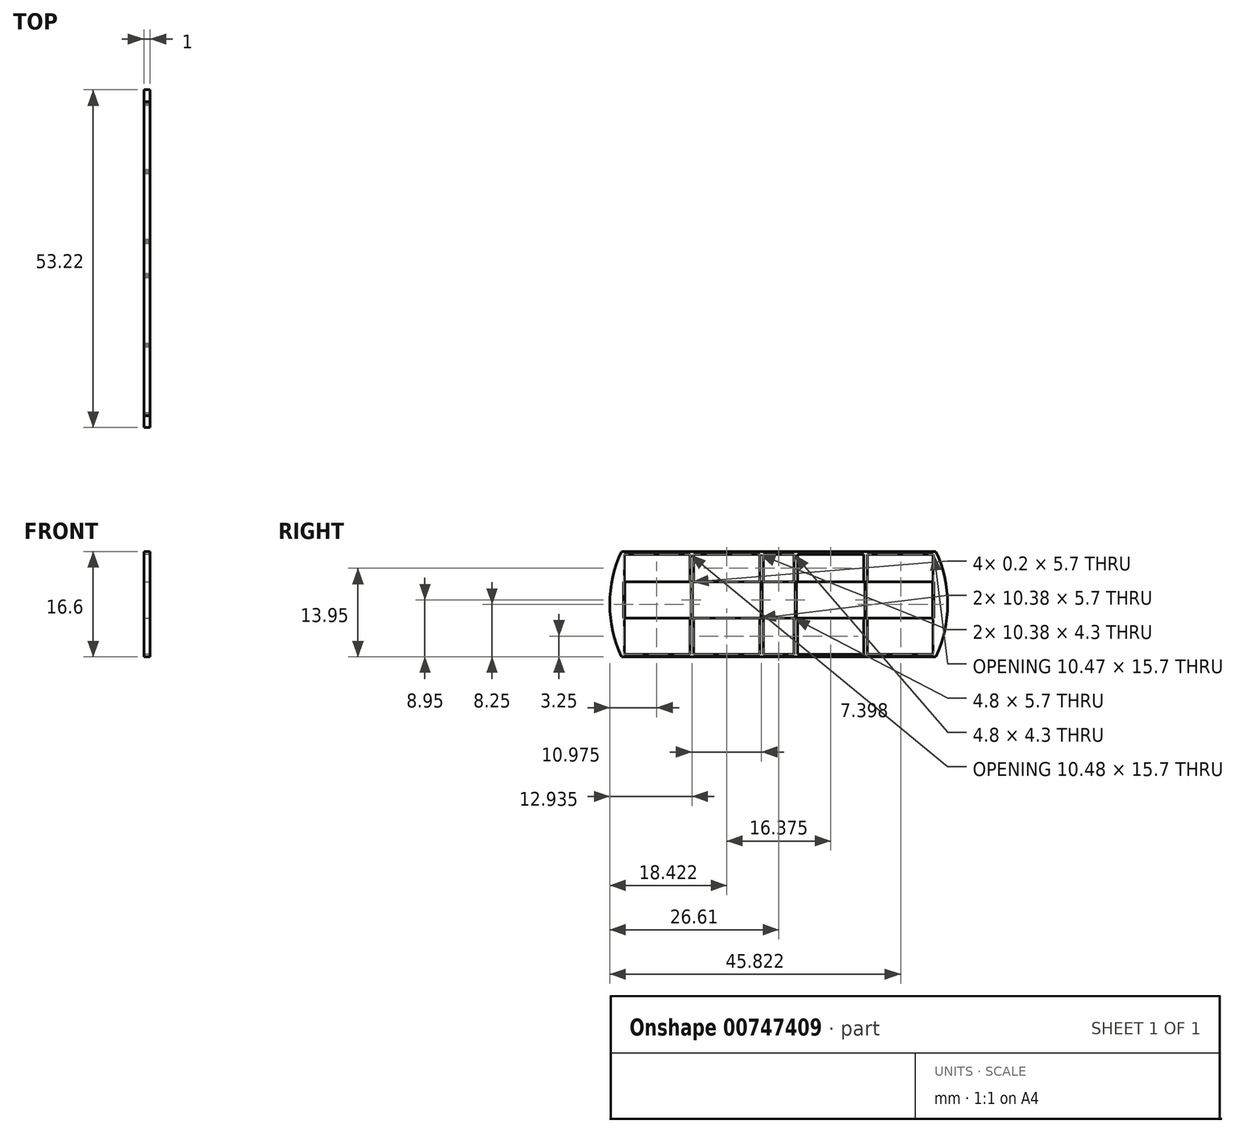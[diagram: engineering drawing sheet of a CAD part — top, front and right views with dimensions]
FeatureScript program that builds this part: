
annotation { "Feature Type Name" : "Feature", "Feature Type Description" : "" }
export const myFeature = defineFeature(function(context is Context, id is Id, definition is map)
    precondition{}
    {
        {
            var Q0;
            Q0=qCreatedBy(makeId("Right.planeOp"),FACE);
            var sketch = newSketch(context, id + "F0", { "sketchPlane" : qUnion([Q0])});
            skLineSegment(sketch, "E0.bottom", {"start": v(0, 0) * mm, "end": v(-49.5, 0) * mm});
            skLineSegment(sketch, "E0.top", {"start": v(0, 16.6) * mm, "end": v(-49.5, 16.6) * mm});
            skLineSegment(sketch, "E0.left", {"start": v(0, 0) * mm, "end": v(0, 16.6) * mm, "construction": true});
            skLineSegment(sketch, "E0.right", {"start": v(-49.5, 0) * mm, "end": v(-49.5, 16.6) * mm, "construction": true});
            skArc(sketch, "E1", {"start": v(-49.5, 0) * mm, "mid": v(-51.36, 8.3) * mm, "end": v(-49.5, 16.6) * mm});
            skPoint(sketch, "E1.centerSnap0", {"position": v(-49.5, 8.3) * mm});
            skArc(sketch, "E2", {"start": v(0, 0) * mm, "mid": v(1.86, 8.3) * mm, "end": v(0, 16.6) * mm});
            skPoint(sketch, "E2.centerSnap0", {"position": v(0, 8.3) * mm});
            skLineSegment(sketch, "E3", {"start": v(-49.5, 8.3) * mm, "end": v(-51.36, 8.3) * mm, "construction": true});
            skLineSegment(sketch, "E4", {"start": v(0, 8.3) * mm, "end": v(1.86, 8.3) * mm, "construction": true});
            skLineSegment(sketch, "E5.bottom", {"start": v(-49.1, 16.1) * mm, "end": v(-38.73, 16.1) * mm});
            skLineSegment(sketch, "E5.top", {"start": v(-49.1, 11.8) * mm, "end": v(-38.73, 11.8) * mm});
            skLineSegment(sketch, "E5.left", {"start": v(-49.1, 16.1) * mm, "end": v(-49.1, 11.8) * mm});
            skLineSegment(sketch, "E5.right", {"start": v(-38.73, 16.1) * mm, "end": v(-38.73, 11.8) * mm});
            skLineSegment(sketch, "E6.bottom", {"start": v(-38.12, 16.1) * mm, "end": v(-27.75, 16.1) * mm});
            skLineSegment(sketch, "E6.top", {"start": v(-38.12, 11.8) * mm, "end": v(-27.75, 11.8) * mm});
            skLineSegment(sketch, "E6.left", {"start": v(-38.12, 16.1) * mm, "end": v(-38.12, 11.8) * mm});
            skLineSegment(sketch, "E6.right", {"start": v(-27.75, 16.1) * mm, "end": v(-27.75, 11.8) * mm});
            skLineSegment(sketch, "E7.bottom", {"start": v(-27.15, 16.1) * mm, "end": v(-22.35, 16.1) * mm});
            skLineSegment(sketch, "E7.top", {"start": v(-27.15, 11.8) * mm, "end": v(-22.35, 11.8) * mm});
            skLineSegment(sketch, "E7.left", {"start": v(-27.15, 16.1) * mm, "end": v(-27.15, 11.8) * mm});
            skLineSegment(sketch, "E7.right", {"start": v(-22.35, 16.1) * mm, "end": v(-22.35, 11.8) * mm});
            skLineSegment(sketch, "E8.bottom", {"start": v(-21.75, 16.1) * mm, "end": v(-11.38, 16.1) * mm});
            skLineSegment(sketch, "E8.top", {"start": v(-21.75, 11.8) * mm, "end": v(-11.38, 11.8) * mm});
            skLineSegment(sketch, "E8.left", {"start": v(-21.75, 16.1) * mm, "end": v(-21.75, 11.8) * mm});
            skLineSegment(sketch, "E8.right", {"start": v(-11.38, 16.1) * mm, "end": v(-11.38, 11.8) * mm});
            skLineSegment(sketch, "E9.bottom", {"start": v(-10.78, 16.1) * mm, "end": v(-0.4, 16.1) * mm});
            skLineSegment(sketch, "E9.top", {"start": v(-10.78, 11.8) * mm, "end": v(-0.4, 11.8) * mm});
            skLineSegment(sketch, "E9.left", {"start": v(-10.78, 16.1) * mm, "end": v(-10.78, 11.8) * mm});
            skLineSegment(sketch, "E9.right", {"start": v(-0.4, 16.1) * mm, "end": v(-0.4, 11.8) * mm});
            skLineSegment(sketch, "E10.bottom", {"start": v(-49.1, 6.1) * mm, "end": v(-38.73, 6.1) * mm});
            skLineSegment(sketch, "E10.top", {"start": v(-49.1, 0.4) * mm, "end": v(-38.73, 0.4) * mm});
            skLineSegment(sketch, "E10.left", {"start": v(-49.1, 6.1) * mm, "end": v(-49.1, 0.4) * mm});
            skLineSegment(sketch, "E10.right", {"start": v(-38.73, 6.1) * mm, "end": v(-38.73, 0.4) * mm});
            skLineSegment(sketch, "E11.bottom", {"start": v(-38.12, 6.1) * mm, "end": v(-27.75, 6.1) * mm});
            skLineSegment(sketch, "E11.top", {"start": v(-38.12, 0.4) * mm, "end": v(-27.75, 0.4) * mm});
            skLineSegment(sketch, "E11.left", {"start": v(-38.12, 6.1) * mm, "end": v(-38.12, 0.4) * mm});
            skLineSegment(sketch, "E11.right", {"start": v(-27.75, 6.1) * mm, "end": v(-27.75, 0.4) * mm});
            skLineSegment(sketch, "E12.bottom", {"start": v(-27.15, 6.1) * mm, "end": v(-22.35, 6.1) * mm});
            skLineSegment(sketch, "E12.top", {"start": v(-27.15, 0.4) * mm, "end": v(-22.35, 0.4) * mm});
            skLineSegment(sketch, "E12.left", {"start": v(-27.15, 6.1) * mm, "end": v(-27.15, 0.4) * mm});
            skLineSegment(sketch, "E12.right", {"start": v(-22.35, 6.1) * mm, "end": v(-22.35, 0.4) * mm});
            skLineSegment(sketch, "E13.bottom", {"start": v(-21.75, 6.1) * mm, "end": v(-11.38, 6.1) * mm});
            skLineSegment(sketch, "E13.top", {"start": v(-21.75, 0.4) * mm, "end": v(-11.38, 0.4) * mm});
            skLineSegment(sketch, "E13.left", {"start": v(-21.75, 6.1) * mm, "end": v(-21.75, 0.4) * mm});
            skLineSegment(sketch, "E13.right", {"start": v(-11.38, 6.1) * mm, "end": v(-11.38, 0.4) * mm});
            skLineSegment(sketch, "E14.bottom", {"start": v(-10.78, 6.1) * mm, "end": v(-0.4, 6.1) * mm});
            skLineSegment(sketch, "E14.top", {"start": v(-10.78, 0.4) * mm, "end": v(-0.4, 0.4) * mm});
            skLineSegment(sketch, "E14.left", {"start": v(-10.78, 6.1) * mm, "end": v(-10.78, 0.4) * mm});
            skLineSegment(sketch, "E14.right", {"start": v(-0.4, 6.1) * mm, "end": v(-0.4, 0.4) * mm});
            skLineSegment(sketch, "E15", {"start": v(-38.73, 13.95) * mm, "end": v(-38.12, 13.95) * mm, "construction": true});
            skLineSegment(sketch, "E16", {"start": v(-27.75, 13.95) * mm, "end": v(-27.15, 13.95) * mm, "construction": true});
            skLineSegment(sketch, "E17", {"start": v(-22.35, 13.95) * mm, "end": v(-21.75, 13.95) * mm, "construction": true});
            skLineSegment(sketch, "E18", {"start": v(-11.38, 13.95) * mm, "end": v(-10.78, 13.95) * mm, "construction": true});
            skSolve(sketch);
        }
        {
            var Q0;
            Q0 = qSketchRegion(id + "F0", true);
            extrude(context, id + "F1", {"entities" : qUnion([Q0]), "depth" : 1 * mm, "offsetDistance" : 25 * mm});
        }
        {
            var Q0;
            Q0=makeQuery(id+"F1.opExtrude","CAP_FACE",FACE,{"disambiguationData":[OSD([sQuery(id+"F0.wireOp",EDGE,"E0.bottom"),sQuery(id+"F0.wireOp",EDGE,"E0.top"),sQuery(id+"F0.wireOp",EDGE,"E1"),sQuery(id+"F0.wireOp",EDGE,"E2"),sQuery(id+"F0.wireOp",EDGE,"E5.bottom"),sQuery(id+"F0.wireOp",EDGE,"E5.top"),sQuery(id+"F0.wireOp",EDGE,"E5.left"),sQuery(id+"F0.wireOp",EDGE,"E5.right"),sQuery(id+"F0.wireOp",EDGE,"E6.bottom"),sQuery(id+"F0.wireOp",EDGE,"E6.top"),sQuery(id+"F0.wireOp",EDGE,"E6.left"),sQuery(id+"F0.wireOp",EDGE,"E6.right"),sQuery(id+"F0.wireOp",EDGE,"E7.bottom"),sQuery(id+"F0.wireOp",EDGE,"E7.top"),sQuery(id+"F0.wireOp",EDGE,"E7.left"),sQuery(id+"F0.wireOp",EDGE,"E7.right"),sQuery(id+"F0.wireOp",EDGE,"E8.bottom"),sQuery(id+"F0.wireOp",EDGE,"E8.top"),sQuery(id+"F0.wireOp",EDGE,"E8.left"),sQuery(id+"F0.wireOp",EDGE,"E8.right"),sQuery(id+"F0.wireOp",EDGE,"E9.bottom"),sQuery(id+"F0.wireOp",EDGE,"E9.top"),sQuery(id+"F0.wireOp",EDGE,"E9.left"),sQuery(id+"F0.wireOp",EDGE,"E9.right"),sQuery(id+"F0.wireOp",EDGE,"E10.bottom"),sQuery(id+"F0.wireOp",EDGE,"E10.top"),sQuery(id+"F0.wireOp",EDGE,"E10.left"),sQuery(id+"F0.wireOp",EDGE,"E10.right"),sQuery(id+"F0.wireOp",EDGE,"E11.bottom"),sQuery(id+"F0.wireOp",EDGE,"E11.top"),sQuery(id+"F0.wireOp",EDGE,"E11.left"),sQuery(id+"F0.wireOp",EDGE,"E11.right"),sQuery(id+"F0.wireOp",EDGE,"E12.bottom"),sQuery(id+"F0.wireOp",EDGE,"E12.top"),sQuery(id+"F0.wireOp",EDGE,"E12.left"),sQuery(id+"F0.wireOp",EDGE,"E12.right"),sQuery(id+"F0.wireOp",EDGE,"E13.bottom"),sQuery(id+"F0.wireOp",EDGE,"E13.top"),sQuery(id+"F0.wireOp",EDGE,"E13.left"),sQuery(id+"F0.wireOp",EDGE,"E13.right"),sQuery(id+"F0.wireOp",EDGE,"E14.bottom"),sQuery(id+"F0.wireOp",EDGE,"E14.top"),sQuery(id+"F0.wireOp",EDGE,"E14.left"),sQuery(id+"F0.wireOp",EDGE,"E14.right")])],"isStart":false});
            var sketch = newSketch(context, id + "F2", { "sketchPlane" : qUnion([Q0])});
            skLineSegment(sketch, "E19.bottom", {"start": v(-49.2, 11.8) * mm, "end": v(-49, 11.8) * mm});
            skLineSegment(sketch, "E19.top", {"start": v(-49.2, 6.1) * mm, "end": v(-49, 6.1) * mm});
            skLineSegment(sketch, "E19.left", {"start": v(-49.2, 11.8) * mm, "end": v(-49.2, 6.1) * mm});
            skLineSegment(sketch, "E19.right", {"start": v(-49, 11.8) * mm, "end": v(-49, 6.1) * mm});
            skLineSegment(sketch, "E20.bottom", {"start": v(-38.32, 11.8) * mm, "end": v(-38.53, 11.8) * mm});
            skLineSegment(sketch, "E20.top", {"start": v(-38.32, 6.1) * mm, "end": v(-38.53, 6.1) * mm});
            skLineSegment(sketch, "E20.left", {"start": v(-38.32, 11.8) * mm, "end": v(-38.32, 6.1) * mm});
            skLineSegment(sketch, "E20.right", {"start": v(-38.53, 11.8) * mm, "end": v(-38.53, 6.1) * mm});
            skLineSegment(sketch, "E21.bottom", {"start": v(-27.35, 11.8) * mm, "end": v(-27.55, 11.8) * mm});
            skLineSegment(sketch, "E21.top", {"start": v(-27.35, 6.1) * mm, "end": v(-27.55, 6.1) * mm});
            skLineSegment(sketch, "E21.left", {"start": v(-27.35, 11.8) * mm, "end": v(-27.35, 6.1) * mm});
            skLineSegment(sketch, "E21.right", {"start": v(-27.55, 11.8) * mm, "end": v(-27.55, 6.1) * mm});
            skLineSegment(sketch, "E22.bottom", {"start": v(-21.95, 11.8) * mm, "end": v(-22.15, 11.8) * mm});
            skLineSegment(sketch, "E22.top", {"start": v(-21.95, 6.1) * mm, "end": v(-22.15, 6.1) * mm});
            skLineSegment(sketch, "E22.left", {"start": v(-22.15, 11.8) * mm, "end": v(-22.15, 6.1) * mm});
            skLineSegment(sketch, "E22.right", {"start": v(-21.95, 11.8) * mm, "end": v(-21.95, 6.1) * mm});
            skLineSegment(sketch, "E23.bottom", {"start": v(-10.98, 11.8) * mm, "end": v(-11.18, 11.8) * mm});
            skLineSegment(sketch, "E23.top", {"start": v(-10.97, 6.1) * mm, "end": v(-11.17, 6.1) * mm});
            skLineSegment(sketch, "E23.left", {"start": v(-10.98, 11.8) * mm, "end": v(-10.97, 6.1) * mm});
            skLineSegment(sketch, "E23.right", {"start": v(-11.18, 11.8) * mm, "end": v(-11.17, 6.1) * mm});
            skLineSegment(sketch, "E24.bottom", {"start": v(-0.3, 11.8) * mm, "end": v(-0.5, 11.8) * mm});
            skLineSegment(sketch, "E24.top", {"start": v(-0.3, 6.1) * mm, "end": v(-0.5, 6.1) * mm});
            skLineSegment(sketch, "E24.left", {"start": v(-0.3, 11.8) * mm, "end": v(-0.3, 6.1) * mm});
            skLineSegment(sketch, "E24.right", {"start": v(-0.5, 11.8) * mm, "end": v(-0.5, 6.1) * mm});
            skLineSegment(sketch, "E25", {"start": v(-38.73, 11.8) * mm, "end": v(-38.53, 11.8) * mm, "construction": true});
            skLineSegment(sketch, "E26", {"start": v(-38.32, 11.8) * mm, "end": v(-38.12, 11.8) * mm, "construction": true});
            skLineSegment(sketch, "E27", {"start": v(-27.75, 11.8) * mm, "end": v(-27.55, 11.8) * mm, "construction": true});
            skLineSegment(sketch, "E28", {"start": v(-27.35, 11.8) * mm, "end": v(-27.15, 11.8) * mm, "construction": true});
            skLineSegment(sketch, "E29", {"start": v(-22.35, 11.8) * mm, "end": v(-22.15, 11.8) * mm, "construction": true});
            skLineSegment(sketch, "E30", {"start": v(-21.95, 11.8) * mm, "end": v(-21.75, 11.8) * mm, "construction": true});
            skLineSegment(sketch, "E31", {"start": v(-11.38, 11.8) * mm, "end": v(-11.18, 11.8) * mm, "construction": true});
            skLineSegment(sketch, "E32", {"start": v(-10.98, 11.8) * mm, "end": v(-10.78, 11.8) * mm, "construction": true});
            skSolve(sketch);
        }
        {
            var Q0;
            Q0 = qSketchRegion(id + "F2", true);
            extrude(context, id + "F3", {"entities" : qUnion([Q0]), "operationType" : NewBodyOperationType.REMOVE, "endBound" : BoundingType.UP_TO_NEXT, "oppositeDirection" : true, "depth" : 25 * mm, "offsetDistance" : 25 * mm});
        }
    });
